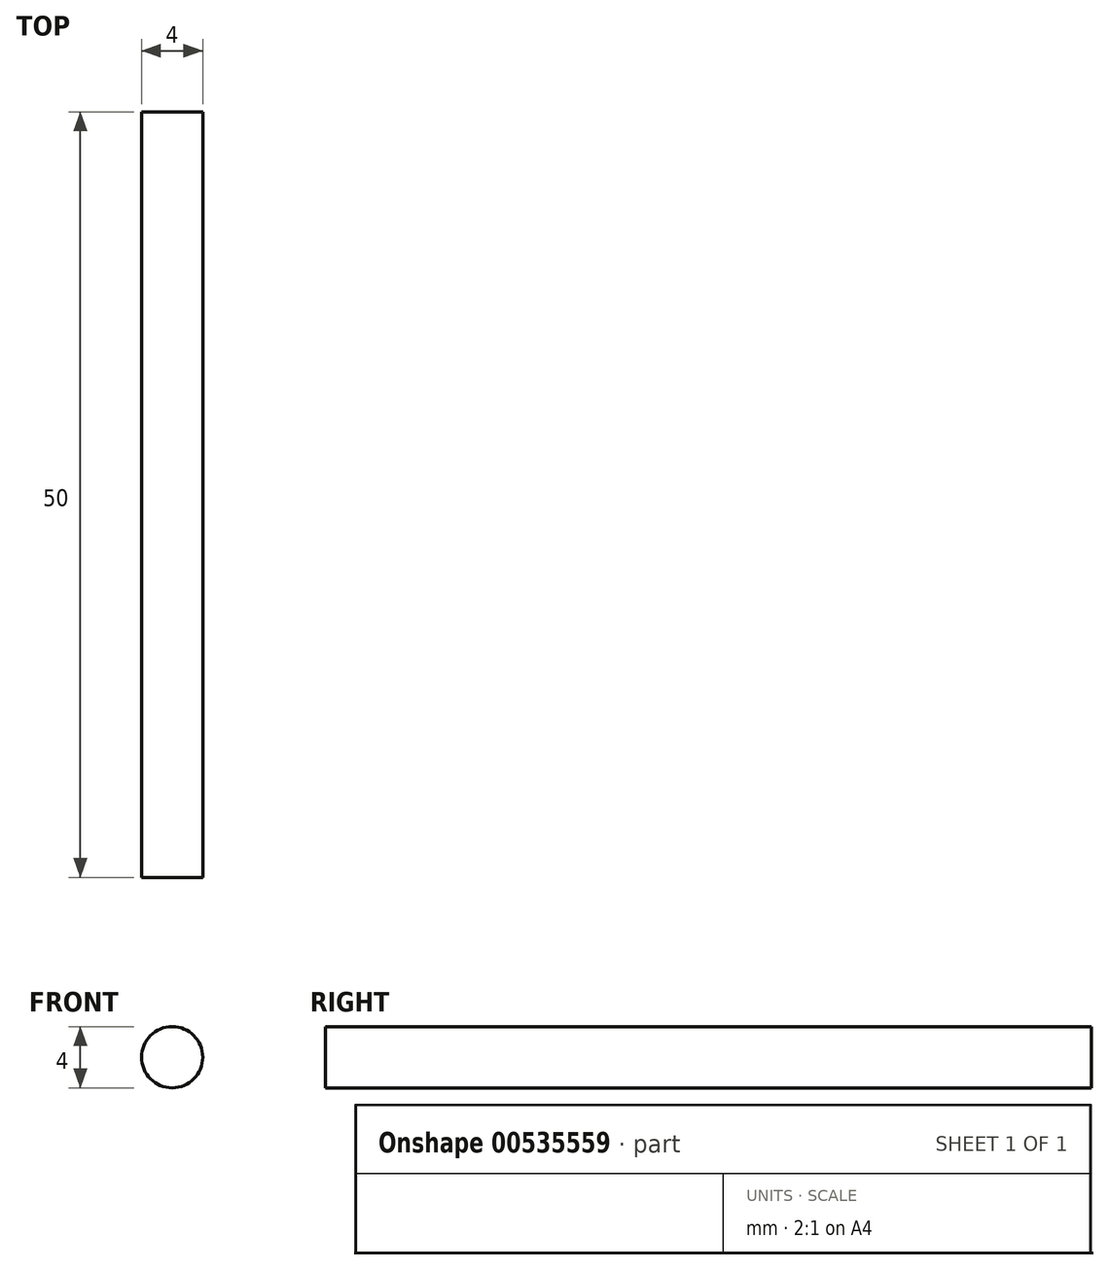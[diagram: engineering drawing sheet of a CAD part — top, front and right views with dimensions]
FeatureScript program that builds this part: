
annotation { "Feature Type Name" : "Feature", "Feature Type Description" : "" }
export const myFeature = defineFeature(function(context is Context, id is Id, definition is map)
    precondition{}
    {
        {
            var Q0;
            Q0=qCreatedBy(makeId("Front.planeOp"),FACE);
            var sketch = newSketch(context, id + "F0", { "sketchPlane" : qUnion([Q0])});
            skCircle(sketch, "E0", {"center": v(0, 0) * mm, "radius": 2 * mm});
            skSolve(sketch);
        }
        {
            var Q0;
            Q0 = qSketchRegion(id + "F0", true);
            extrude(context, id + "F1", {"entities" : qUnion([Q0]), "depth" : 50 * mm, "offsetDistance" : 25 * mm, "symmetric" : true});
        }
    });
